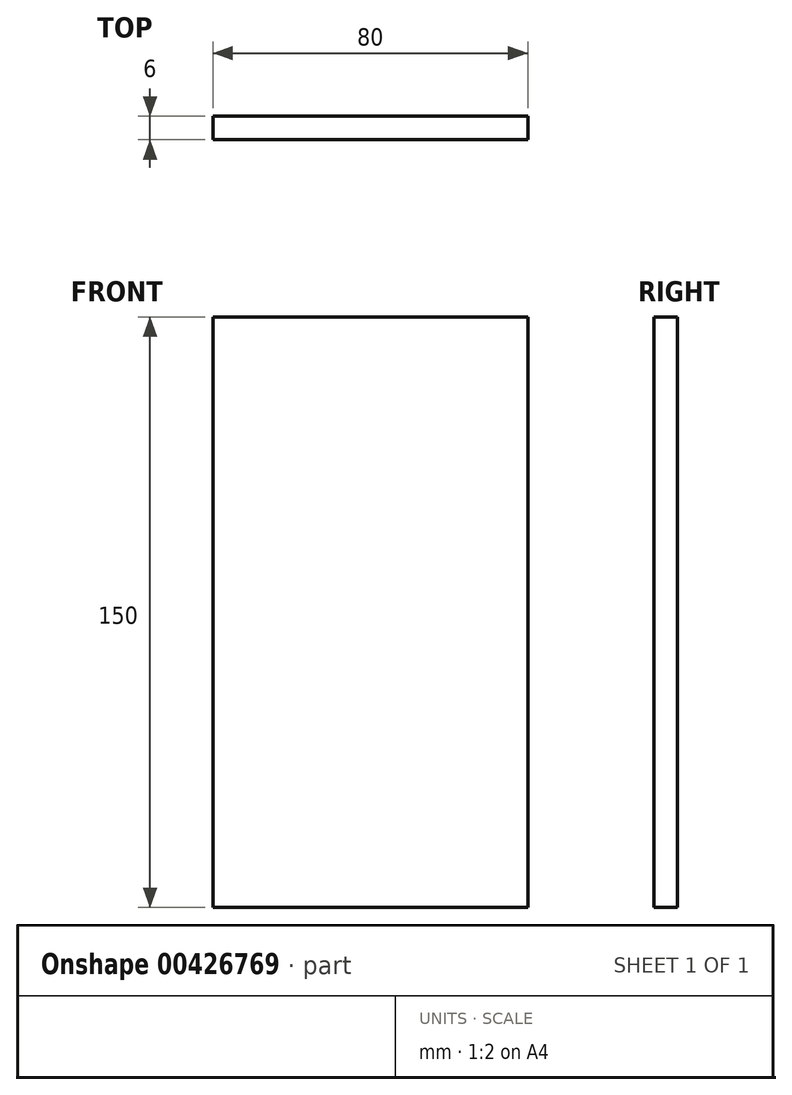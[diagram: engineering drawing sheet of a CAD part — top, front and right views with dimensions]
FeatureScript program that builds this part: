
annotation { "Feature Type Name" : "Feature", "Feature Type Description" : "" }
export const myFeature = defineFeature(function(context is Context, id is Id, definition is map)
    precondition{}
    {
        {
            var Q0;
            Q0=qCreatedBy(makeId("Front.planeOp"),FACE);
            var sketch = newSketch(context, id + "F0", { "sketchPlane" : qUnion([Q0])});
            skLineSegment(sketch, "E0.bottom", {"start": v(-40, 0) * mm, "end": v(40, 0) * mm});
            skLineSegment(sketch, "E0.top", {"start": v(-40, -150) * mm, "end": v(40, -150) * mm});
            skLineSegment(sketch, "E0.left", {"start": v(-40, 0) * mm, "end": v(-40, -150) * mm});
            skLineSegment(sketch, "E0.right", {"start": v(40, 0) * mm, "end": v(40, -150) * mm});
            skSolve(sketch);
        }
        {
            var Q0;
            Q0=makeQuery(id+"F0.imprint","IMPRINT",FACE,{"disambiguationData":[TD([[makeQuery(id+"F0.imprint","IMPRINT",EDGE,{"derivedFrom":sQuery(id+"F0.wireOp",EDGE,"E0.bottom")}),-1.0]])]});
            extrude(context, id + "F1", {"entities" : qUnion([Q0]), "depth" : 6 * mm});
        }
    });
